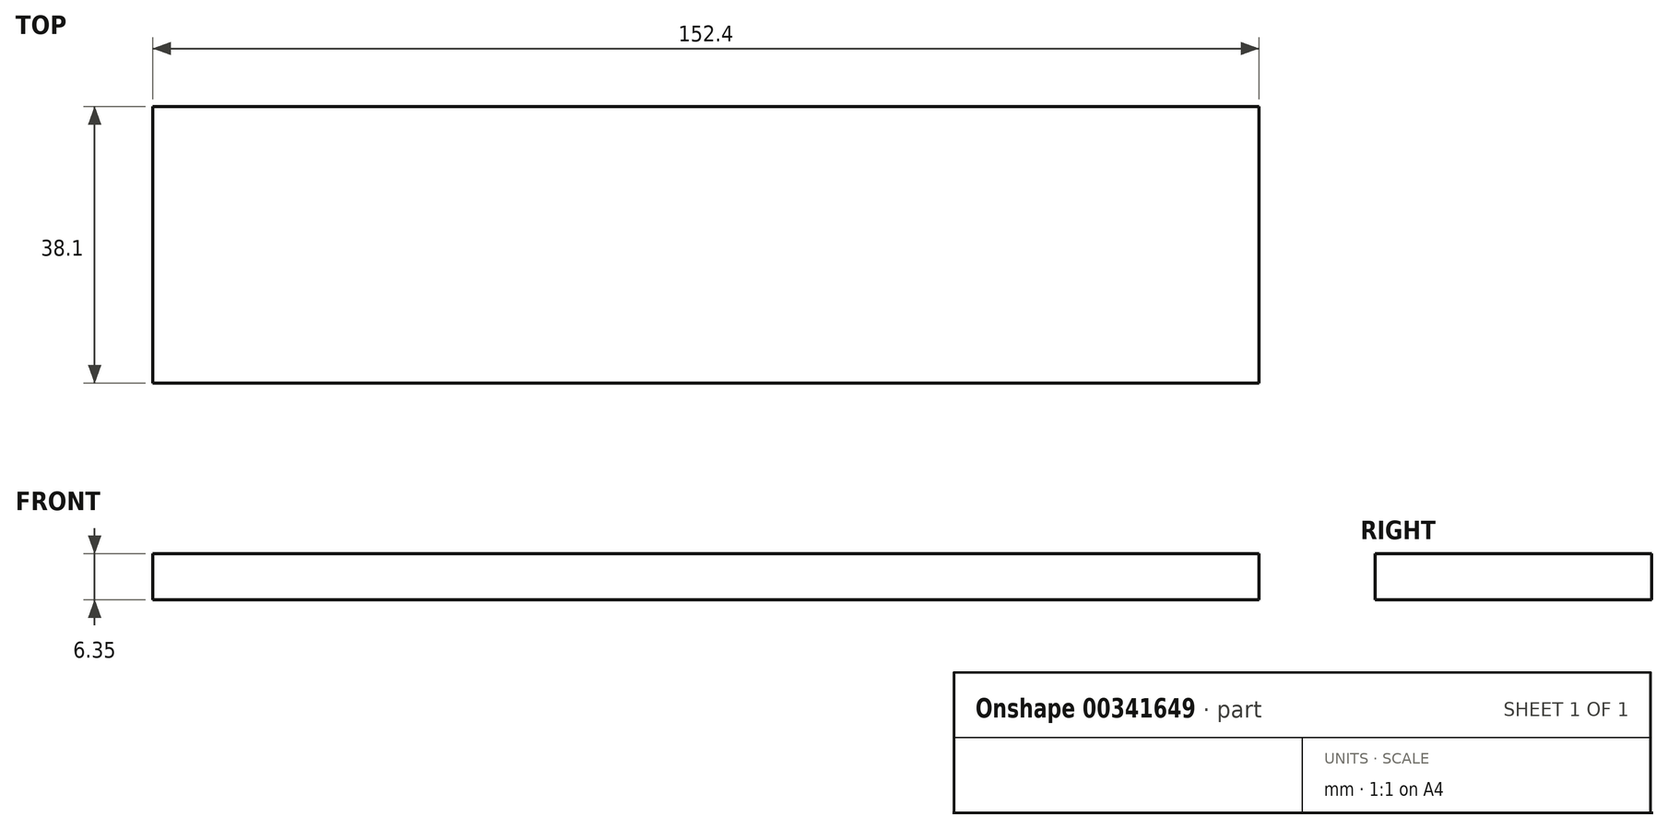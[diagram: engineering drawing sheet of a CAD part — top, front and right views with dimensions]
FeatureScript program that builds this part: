
annotation { "Feature Type Name" : "Feature", "Feature Type Description" : "" }
export const myFeature = defineFeature(function(context is Context, id is Id, definition is map)
    precondition{}
    {
        {
            var Q0;
            Q0=qCreatedBy(makeId("Top.planeOp"),FACE);
            var sketch = newSketch(context, id + "F0", { "sketchPlane" : qUnion([Q0])});
            skLineSegment(sketch, "E0.bottom", {"start": v(76.2, 19.05) * mm, "end": v(-76.2, 19.05) * mm});
            skLineSegment(sketch, "E0.top", {"start": v(76.2, -19.05) * mm, "end": v(-76.2, -19.05) * mm});
            skLineSegment(sketch, "E0.left", {"start": v(76.2, 19.05) * mm, "end": v(76.2, -19.05) * mm});
            skLineSegment(sketch, "E0.right", {"start": v(-76.2, 19.05) * mm, "end": v(-76.2, -19.05) * mm});
            skPoint(sketch, "E0.middle", {"position": v(0, 0) * mm});
            skSolve(sketch);
        }
        {
            var Q0;
            Q0 = qSketchRegion(id + "F0", true);
            extrude(context, id + "F1", {"entities" : qUnion([Q0]), "depth" : 6.35 * mm});
        }
    });
